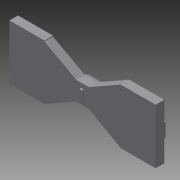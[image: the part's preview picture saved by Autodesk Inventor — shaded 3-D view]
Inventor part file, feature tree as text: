
AUTODESK INVENTOR PART (.ipt)
format: ipt  version: 2014 SP2 (Build 180246200, 246)  size: 217,600 bytes
history: native  units: mm
features: extrude x7, sketch x7, fillet x1
ambient origin geometry x8: Origin, YZ Plane, XZ Plane, XY Plane, X Axis, Y Axis, Z Axis, Center Point
bodies: Solid1 (feature_tree)
feature tree (15):
  extrude  "Extrusion1"  Depth=173.0mm
  extrude  "Extrusion2"  Depth=110.0mm
  extrude  "Extrusion3"  Depth=210.0mm
  extrude  "Extrusion4"  Depth=59.0mm
  extrude  "Extrusion5"  Depth=57.0mm
  fillet  "Fillet1"  [1 undecoded]
  extrude  "Extrusion6"  Depth=30.0mm
  extrude  "Extrusion7"  Depth=15.0mm
  sketch  "Sketch1"  dims[d0=460.0mm d1=173.0mm]
  sketch  "Sketch2"  dims[d2=110.0mm d3=110.0mm]
  sketch  "Sketch3"  dims[d4=210.0mm d5=210.0mm]
  sketch  "Sketch4"  dims[d6=40.0mm d7=59.0mm]
  sketch  "Sketch5"  dims[d8=40.0mm d9=57.0mm d10=0.0mm]
  sketch  "Sketch6"  dims[d11=10.0mm d12=30.0mm]
  sketch  "Sketch7"  dims[d13=14.5mm d14=15.0mm d15=3.0mm d16=0.0mm d17=3.0mm d18=24.0mm d19=0.0mm d20=5.0mm d21=0.0mm d22=49.0mm d23=0.0mm d24=25.0mm d25=0.0mm d26=30.0mm d27=39.0mm d28=44.0mm d29=0.0mm d30=61.5mm d31=61.5mm d32=32.0mm d33=0.0mm d34=39.0mm d35=44.0mm d36=0.0mm d37=61.5mm d38=32.0mm d39=0.0mm]
note: 1 required parameter value undecoded (feature->parameter linkage not recoverable at this tier; creation-order binding heuristic only, values carry confidence <= 0.55)
